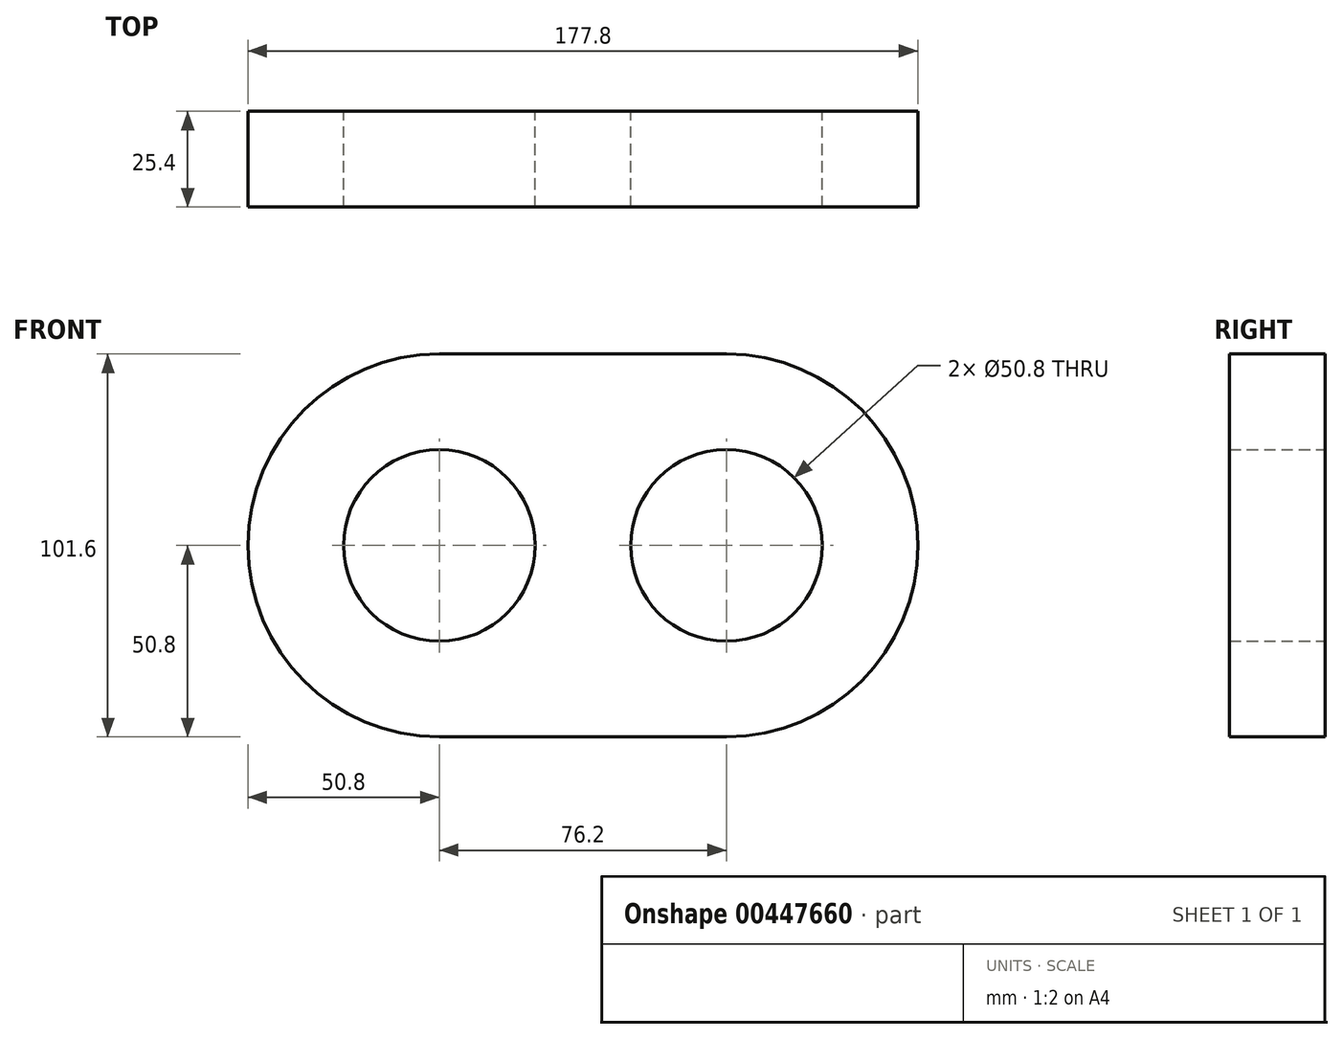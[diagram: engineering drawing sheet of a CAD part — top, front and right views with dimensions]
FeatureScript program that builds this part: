
annotation { "Feature Type Name" : "Feature", "Feature Type Description" : "" }
export const myFeature = defineFeature(function(context is Context, id is Id, definition is map)
    precondition{}
    {
        {
            var Q0;
            Q0=qCreatedBy(makeId("Front.planeOp"),FACE);
            var sketch = newSketch(context, id + "F0", { "sketchPlane" : qUnion([Q0])});
            skCircle(sketch, "E0", {"center": v(0, 0) * mm, "radius": 50.8 * mm});
            skLineSegment(sketch, "E1.bottom", {"start": v(0, 50.8) * mm, "end": v(127, 50.8) * mm});
            skLineSegment(sketch, "E1.top", {"start": v(0, -50.8) * mm, "end": v(127, -50.8) * mm});
            skLineSegment(sketch, "E1.left", {"start": v(0, 50.8) * mm, "end": v(0, -50.8) * mm});
            skLineSegment(sketch, "E1.right", {"start": v(127, 50.8) * mm, "end": v(127, -50.8) * mm});
            skSolve(sketch);
        }
        {
            var Q0;
            Q0 = qSketchRegion(id + "F0", true);
            extrude(context, id + "F1", {"entities" : qUnion([Q0]), "depth" : 25.4 * mm});
        }
        {
            var Q0;
            Q0=makeQuery(id+"F1.opExtrude","SWEPT_EDGE",EDGE,{"disambiguationData":[OSD([sQuery(id+"F0.wireOp",EDGE,"E1.bottom"),sQuery(id+"F0.wireOp",EDGE,"E1.right")])]});
            var Q1;
            Q1=makeQuery(id+"F1.opExtrude","SWEPT_EDGE",EDGE,{"disambiguationData":[OSD([sQuery(id+"F0.wireOp",EDGE,"E1.top"),sQuery(id+"F0.wireOp",EDGE,"E1.right")])]});
            fillet(context, id + "F2", {"entities" : qUnion([Q0, Q1]), "radius" : 50.8 * mm, "tangentPropagation" : true, "allowEdgeOverflow" : false});
        }
        {
            var Q0;
            Q0=qCreatedBy(makeId("Front.planeOp"),FACE);
            var sketch = newSketch(context, id + "F3", { "sketchPlane" : qUnion([Q0])});
            skCircle(sketch, "E2", {"center": v(0, 0) * mm, "radius": 25.4 * mm});
            skSolve(sketch);
        }
        {
            var Q0;
            Q0 = qSketchRegion(id + "F3", true);
            extrude(context, id + "F4", {"entities" : qUnion([Q0]), "operationType" : NewBodyOperationType.REMOVE, "depth" : 79.25 * mm});
        }
        {
            var Q0;
            Q0=qCreatedBy(makeId("Right.planeOp"),FACE);
            cPlane(context, id + "F5", {"entities" : qUnion([Q0]), "cplaneType" : CPlaneType.OFFSET, "offset" : 50.8 * mm, "width" : 152.4 * mm, "height" : 152.4 * mm});
        }
        {
            var Q0;
            Q0=qCreatedBy(id+"F5.planeOp",FACE);
            cPlane(context, id + "F6", {"entities" : qUnion([Q0]), "cplaneType" : CPlaneType.OFFSET, "offset" : 12.7 * mm, "oppositeDirection" : true, "width" : 152.4 * mm, "height" : 152.4 * mm});
        }
        {
            var Q0;
            Q0=makeQuery(id+"F4.boolean.opBoolean","COPY",FACE,{"derivedFrom":makeQuery(id+"F4.opExtrude","SWEPT_FACE",FACE,{"disambiguationData":[OSD([sQuery(id+"F3.wireOp",EDGE,"E2")])]})});
            var Q1;
            Q1=qCreatedBy(id+"F6.planeOp",FACE);
            mirror(context, id + "F7", {"patternType" : MirrorType.FACE, "faces" : qUnion([Q0]), "mirrorPlane" : qUnion([Q1])});
        }
    });
